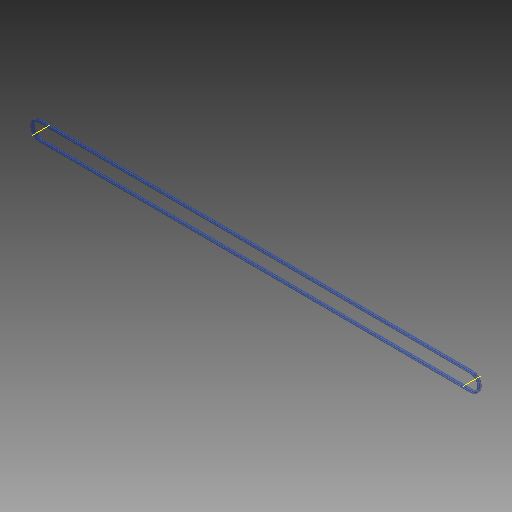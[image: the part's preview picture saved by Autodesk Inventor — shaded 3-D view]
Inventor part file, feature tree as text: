
AUTODESK INVENTOR PART (.ipt)
format: ipt  version: 2017 (Build 210142000, 142)  size: 136,192 bytes
history: native  units: mm
features: other x5, plane x2, pattern_linear x1
ambient origin geometry x8: Origin, YZ Plane, XZ Plane, XY Plane, X Axis, Y Axis, Z Axis, Center Point
bodies: Solid1 (feature_tree), Solid (feature_tree)
feature tree (8):
  other  "Work Axis1"
  other  "Work Axis2"
  plane  "Work Plane2"
  plane  "Work Plane3"
  other  "Path"
  other  "Section Plane"
  pattern_linear  "Strand Pattern"  Spacing1=0.0mm  [1 undecoded]
  other  "Section Sketch"
note: 1 required parameter value undecoded (feature->parameter linkage not recoverable at this tier; creation-order binding heuristic only, values carry confidence <= 0.55)
